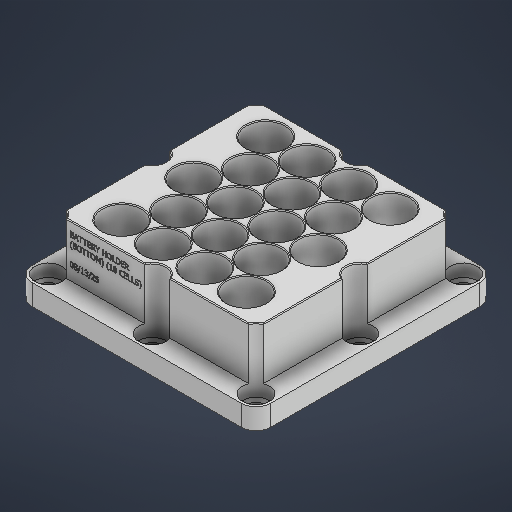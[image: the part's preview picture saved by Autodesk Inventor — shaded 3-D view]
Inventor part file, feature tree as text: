
AUTODESK INVENTOR PART (.ipt)
format: ipt  version: 2025 (Build 290162000, 162)  size: 1,085,440 bytes
history: native  units: in
note: dims shown in document units (in); Inventor stores cm internally (conversion verified against a paired STEP export)
features: sketch x7, extrude x3, hole x1, fillet x1, chamfer x1
ambient origin geometry x8: Origin, YZ Plane, XZ Plane, XY Plane, X Axis, Y Axis, Z Axis, Center Point
bodies: Solid1 (feature_tree)
feature tree (13):
  extrude  "Extrusion1"  Depth=4.5276in
  extrude  "Extrusion2"  Depth=3.7402in
  hole  "Hole3"  [1 undecoded]
  fillet  "Fillet1"  Radius=1.3638in
  chamfer  "Chamfer1"  Distance=0.748in
  extrude  "Extrusion3"  Depth=0.3937in
  sketch  "Sketch1"  dims[d0=4.5276in d1=4.5276in]
  sketch  "Sketch4"  dims[d2=0.3937in d3=0.0in d48=3.7402in]
  sketch  "Sketch Rectangular Pattern11"  dims[d133=2.7276in]
  sketch  "Sketch Rectangular Pattern12"  dims[d134=0.748in]
  sketch  "Sketch5"  dims[d49=3.7402in d57=0.9843in d58=0.0in d124=1.3638in]
  sketch  "Sketch Rectangular Pattern13"  dims[d135=1.5748in d137=0.7874in d138=1.1811in d140=1.3638in d143=0.748in d146=0.3937in d147=0.6819in d148=1.1811in d150=0.7874in d151=0.7874in d153=1.3638in d156=3.937in d157=3.937in d158=0.2756in d159=1.1811in d161=1.9685in d162=1.1811in d164=1.9685in d167=0.2805in d168=0.2362in d169=0.5118in d170=1.2205in d171=90.0deg d172=0.315in d173=0.8108in d174=0.2805in d175=0.0157in d176=0.0787in d177=45.0deg d178=0.0787in d179=0.0in]
  sketch  "Sketch6"  dims[d132=2.3622in]
note: 1 required parameter value undecoded (feature->parameter linkage not recoverable at this tier; creation-order binding heuristic only, values carry confidence <= 0.55)
